annotation { "Feature Type Name" : "Feature", "Feature Type Description" : "" }
export const myFeature = defineFeature(function(context is Context, id is Id, definition is map)
    precondition{}
    {
        {
            var Q0;
            Q0=qCreatedBy(makeId("Top.planeOp"),FACE);
            var sketch = newSketch(context, id + "F0", { "sketchPlane" : qUnion([Q0])});
            skLineSegment(sketch, "E0.bottom", {"start": v(-41.32, 42.35) * mm, "end": v(47.58, 42.35) * mm});
            skLineSegment(sketch, "E0.top", {"start": v(-41.32, -46.55) * mm, "end": v(47.58, -46.55) * mm});
            skLineSegment(sketch, "E0.left", {"start": v(-41.32, 42.35) * mm, "end": v(-41.32, -46.55) * mm});
            skLineSegment(sketch, "E0.right", {"start": v(47.58, 42.35) * mm, "end": v(47.58, -46.55) * mm});
            skSolve(sketch);
        }
        {
            var Q0;
            Q0=qCreatedBy(makeId("Top.planeOp"),FACE);
            cPlane(context, id + "F1", {"entities" : qUnion([Q0]), "cplaneType" : CPlaneType.OFFSET, "offset" : 88.9 * mm, "width" : 152.4 * mm, "height" : 152.4 * mm});
        }
        {
            var Q0;
            Q0=qCreatedBy(id+"F1.planeOp",FACE);
            var sketch = newSketch(context, id + "F2", { "sketchPlane" : qUnion([Q0])});
            skPoint(sketch, "E1", {"position": v(0, 0) * mm});
            skSolve(sketch);
        }
        {
            var Q0;
            Q0=makeQuery(id+"F0.imprint","IMPRINT",FACE,{"disambiguationData":[TD([[makeQuery(id+"F0.imprint","IMPRINT",EDGE,{"derivedFrom":sQuery(id+"F0.wireOp",EDGE,"E0.bottom")}),-1.0]])]});
            var Q1;
            Q1=sQuery(id+"F2.wireOp",VERTEX,"E1");
            loft(context, id + "F3", {"sheetProfilesArray" : [{ "sheetProfileEntities" : qUnion([Q0]) }, { "sheetProfileEntities" : qUnion([Q1]) }]});
        }
        {
            var Q0;
            Q0=makeQuery(id+"F3.opLoft","SWEPT_FACE",FACE,{"disambiguationData":[OSD([sQuery(id+"F0.wireOp",EDGE,"E0.top"),sQuery(id+"F0.wireOp",EDGE,"E0.left"),sQuery(id+"F0.wireOp",EDGE,"E0.right")])]});
            var sketch = newSketch(context, id + "F4", { "sketchPlane" : qUnion([Q0])});
            skFitSpline(sketch, "E2", {"points": [v(-6.98, 54.06) * mm, v(-3.92, 56.06) * mm, v(0, 56.7) * mm], "startDerivative": vector(5.9, 4.78) * mm, "endDerivative": vector(8.04, 0.51) * mm});
            skFitSpline(sketch, "E3", {"points": [v(-6.98, 50.57) * mm, v(-3.3, 52.98) * mm, v(-1.17, 53.55) * mm, v(0, 53.65) * mm], "startDerivative": vector(8.5, 6.32) * mm, "endDerivative": vector(4.75, 0.26) * mm});
            skFitSpline(sketch, "E4", {"points": [v(-6.98, 50.57) * mm, v(-3.3, 48.17) * mm, v(-1.17, 47.6) * mm, v(0, 47.5) * mm], "startDerivative": vector(8.5, -6.32) * mm, "endDerivative": vector(4.75, -0.26) * mm});
            skFitSpline(sketch, "E5.MirrorCS", {"points": [v(6.98, 50.57) * mm, v(3.3, 52.98) * mm, v(1.17, 53.55) * mm, v(0, 53.65) * mm], "startDerivative": vector(-8.5, 6.32) * mm, "endDerivative": vector(-4.75, 0.26) * mm});
            skFitSpline(sketch, "E6.MirrorCS", {"points": [v(6.98, 50.57) * mm, v(3.3, 48.17) * mm, v(1.17, 47.6) * mm, v(0, 47.5) * mm], "startDerivative": vector(-8.5, -6.32) * mm, "endDerivative": vector(-4.75, -0.26) * mm});
            skFitSpline(sketch, "E7.MirrorCS", {"points": [v(6.98, 54.06) * mm, v(3.92, 56.06) * mm, v(0, 56.7) * mm], "startDerivative": vector(-5.9, 4.78) * mm, "endDerivative": vector(-8.04, 0.51) * mm});
            skCircle(sketch, "E8", {"center": v(0, 50.57) * mm, "radius": 2.64 * mm});
            skFitSpline(sketch, "E9", {"points": [v(-6.98, 54) * mm, v(-3.92, 55.91) * mm, v(0, 56.56) * mm], "startDerivative": vector(5.94, 4.55) * mm, "endDerivative": vector(8, 0.58) * mm});
            skLineSegment(sketch, "E10", {"start": v(0, 59.62) * mm, "end": v(0, 55.05) * mm});
            skFitSpline(sketch, "E11.MirrorCS", {"points": [v(6.98, 54) * mm, v(3.92, 55.91) * mm, v(0, 56.56) * mm], "startDerivative": vector(-5.94, 4.55) * mm, "endDerivative": vector(-8, 0.58) * mm});
            skLineSegment(sketch, "E12", {"start": v(-6.98, 54.06) * mm, "end": v(-6.98, 54) * mm});
            skLineSegment(sketch, "E13", {"start": v(6.98, 54.06) * mm, "end": v(6.98, 54) * mm});
            skCircle(sketch, "E14", {"center": v(0, 50.57) * mm, "radius": 0.89 * mm});
            skSolve(sketch);
        }
        {
            var Q0;
            Q0 = qSketchRegion(id + "F4", true);
            var Q1;
            Q1=makeQuery(id+"F4.imprint","IMPRINT",FACE,{"disambiguationData":[TD([[makeQuery(id+"F4.imprint","IMPRINT",EDGE,{"derivedFrom":sQuery(id+"F4.wireOp",EDGE,"E14")}),1.0]])]});
            extrude(context, id + "F5", {"entities" : qUnion([Q0, Q1]), "operationType" : NewBodyOperationType.ADD, "depth" : 2.54 * mm});
        }
        {
            var Q0;
            Q0=makeQuery(id+"F3.opLoft","CAP_FACE",FACE,{"disambiguationData":[OSD([makeQuery(id+"F0.imprint","IMPRINT",FACE,{"disambiguationData":[TD([[makeQuery(id+"F0.imprint","IMPRINT",EDGE,{"derivedFrom":sQuery(id+"F0.wireOp",EDGE,"E0.bottom")}),-1.0]])]})])],"isStart":true});
            shell(context, id + "F6", {"entities" : qUnion([Q0]), "thickness" : 2.54 * mm});
        }
        {
            var Q0;
            {var subQ0=sQuery(id+"F0.wireOp",EDGE,"E0.left");var subQ1=sQuery(id+"F0.wireOp",EDGE,"E0.top");var subQ3=sQuery(id+"F0.wireOp",EDGE,"E0.right");Q0=makeQuery(id+"F5.boolean.opBoolean","SPLIT",FACE,{"disambiguationData":[TD([makeQuery(id+"F5.opExtrude","SWEPT_FACE",FACE,{"disambiguationData":[OSD([sQuery(id+"F4.wireOp",EDGE,"E2")])]})])],"derivedFrom":makeQuery(id+"F3.opLoft","SWEPT_FACE",FACE,{"disambiguationData":[OSD([subQ1,subQ0,subQ3])]})});}
            var sketch = newSketch(context, id + "F7", { "sketchPlane" : qUnion([Q0])});
            skLineSegment(sketch, "E15.bottom", {"start": v(-17.82, 27.34) * mm, "end": v(20.28, 27.34) * mm});
            skLineSegment(sketch, "E15.top", {"start": v(-17.82, 7.02) * mm, "end": v(20.28, 7.02) * mm});
            skLineSegment(sketch, "E15.left", {"start": v(-17.82, 27.34) * mm, "end": v(-17.82, 7.02) * mm});
            skLineSegment(sketch, "E15.right", {"start": v(20.28, 27.34) * mm, "end": v(20.28, 7.02) * mm});
            skSolve(sketch);
        }
        {
            var Q0;
            Q0 = qSketchRegion(id + "F7", true);
            extrude(context, id + "F8", {"entities" : qUnion([Q0]), "operationType" : NewBodyOperationType.REMOVE, "oppositeDirection" : true, "depth" : 95.43 * mm});
        }
        {
            var Q0;
            {var subQ0=sQuery(id+"F0.wireOp",EDGE,"E0.right");var subQ1=sQuery(id+"F0.wireOp",EDGE,"E0.left");var subQ2=sQuery(id+"F0.wireOp",EDGE,"E0.bottom");Q0=makeQuery(id+"F8.boolean.opBoolean","COPY",FACE,{"disambiguationData":[TD([makeQuery(id+"F3.opLoft","SWEPT_FACE",FACE,{"disambiguationData":[OSD([subQ2,subQ1,subQ0])]})])],"derivedFrom":makeQuery(id+"F8.opExtrude","SWEPT_FACE",FACE,{"disambiguationData":[OSD([sQuery(id+"F7.wireOp",EDGE,"E15.bottom")])]})});}
            shell(context, id + "F9", {"entities" : qUnion([Q0]), "thickness" : 0.25 * mm});
        }
        {
            var Q0;
            Q0=makeQuery(id+"F3.opLoft","SWEPT_FACE",FACE,{"disambiguationData":[OSD([sQuery(id+"F0.wireOp",EDGE,"E0.bottom"),sQuery(id+"F0.wireOp",EDGE,"E0.left"),sQuery(id+"F0.wireOp",EDGE,"E0.right")])]});
            var sketch = newSketch(context, id + "F10", { "sketchPlane" : qUnion([Q0])});
            skLineSegment(sketch, "E16", {"start": v(-20.28, -5.4) * mm, "end": v(-20.28, -18.22) * mm});
            skSolve(sketch);
        }
        {
            var Q0;
            Q0=makeQuery(id+"F5.opExtrude","CAP_EDGE",EDGE,{"disambiguationData":[OSD([sQuery(id+"F4.wireOp",EDGE,"E14")])],"isStart":false});
            fillet(context, id + "F11", {"entities" : qUnion([Q0]), "radius" : 0.76 * mm, "tangentPropagation" : true, "allowEdgeOverflow" : false});
        }
        {
            var Q0;
            Q0=makeQuery(id+"F3.opLoft","SWEPT_FACE",FACE,{"disambiguationData":[OSD([sQuery(id+"F0.wireOp",EDGE,"E0.bottom"),sQuery(id+"F0.wireOp",EDGE,"E0.top"),sQuery(id+"F0.wireOp",EDGE,"E0.right")])]});
            var sketch = newSketch(context, id + "F12", { "sketchPlane" : qUnion([Q0])});
            skText(sketch, "E17", { "text": "Illuminati", "fontName": "RobotoSlab-Regular.ttf"});
            skText(sketch, "E18", { "text": "Confirmed", "fontName": "AllertaStencil-Regular.ttf"});
            skText(sketch, "E19", { "text": "#", "fontName": "OpenSans-Regular.ttf"});
            skText(sketch, "E20", { "text": "Engineering\n   Pathway\n  2015-2016", "fontName": "AllertaStencil-Regular.ttf"});
            const initialGuessF12  = {"E17": [-0.02629, -0.01685, 1, 0, 0.0039], "E18": [0.00061, -0.01652, 1, 0, 0.00353], "E19": [-0.0297, -0.01655, 1, 0, 0.00295], "E20": [-0.02008, 0.02602, 1, 0, 0.00457]};
            skSetInitialGuess(sketch, initialGuessF12);
            skSolve(sketch);
        }
        {
            var Q0;
            Q0 = qSketchRegion(id + "F12", true);
            extrude(context, id + "F13", {"entities" : qUnion([Q0]), "operationType" : NewBodyOperationType.REMOVE, "oppositeDirection" : true, "depth" : 6.55 * mm});
        }
        {
            var Q0;
            Q0=makeQuery(id+"F10.imprint","IMPRINT",FACE,{"disambiguationData":[TD([[makeQuery(id+"F10.imprint","IMPRINT",EDGE,{"derivedFrom":sQuery(id+"F10.wireOp",EDGE,"E16")}),1.0]])]});
            var sketch = newSketch(context, id + "F14", { "sketchPlane" : qUnion([Q0])});
            skText(sketch, "E21", { "text": "Luis", "fontName": "RobotoSlab-Regular.ttf"});
            skText(sketch, "E22", { "text": "Jimenez", "fontName": "RobotoSlab-Regular.ttf"});
            skText(sketch, "E23", { "text": "10", "fontName": "AllertaStencil-Regular.ttf"});
            const initialGuessF14  = {"E21": [-0.01304, 0.032, 1, 0, 0.00921], "E22": [-0.02678, 0.00376, 1, 0, 0.00904], "E23": [-0.00667, 0.01942, 1, 0, 0.00762]};
            skSetInitialGuess(sketch, initialGuessF14);
            skSolve(sketch);
        }
        {
            var Q0;
            Q0 = qSketchRegion(id + "F14", true);
            extrude(context, id + "F15", {"entities" : qUnion([Q0]), "operationType" : NewBodyOperationType.REMOVE, "oppositeDirection" : true, "depth" : 20.1 * mm});
        }
        {
            var Q0;
            Q0=makeQuery(id+"F3.opLoft","SWEPT_FACE",FACE,{"disambiguationData":[OSD([sQuery(id+"F0.wireOp",EDGE,"E0.bottom"),sQuery(id+"F0.wireOp",EDGE,"E0.top"),sQuery(id+"F0.wireOp",EDGE,"E0.left")])]});
            var sketch = newSketch(context, id + "F16", { "sketchPlane" : qUnion([Q0])});
            skText(sketch, "E24", { "text": "FRC", "fontName": "AllertaStencil-Regular.ttf"});
            skText(sketch, "E25", { "text": "2375", "fontName": "AllertaStencil-Regular.ttf"});
            const initialGuessF16  = {"E24": [-0.0156, 0.03021, 1, 0, 0.01322], "E25": [-0.02427, -0.0072, 1, 0, 0.0165]};
            skSetInitialGuess(sketch, initialGuessF16);
            skSolve(sketch);
        }
        {
            var Q0;
            Q0 = qSketchRegion(id + "F16", true);
            extrude(context, id + "F17", {"entities" : qUnion([Q0]), "operationType" : NewBodyOperationType.REMOVE, "oppositeDirection" : true, "depth" : 25.4 * mm});
        }
    });